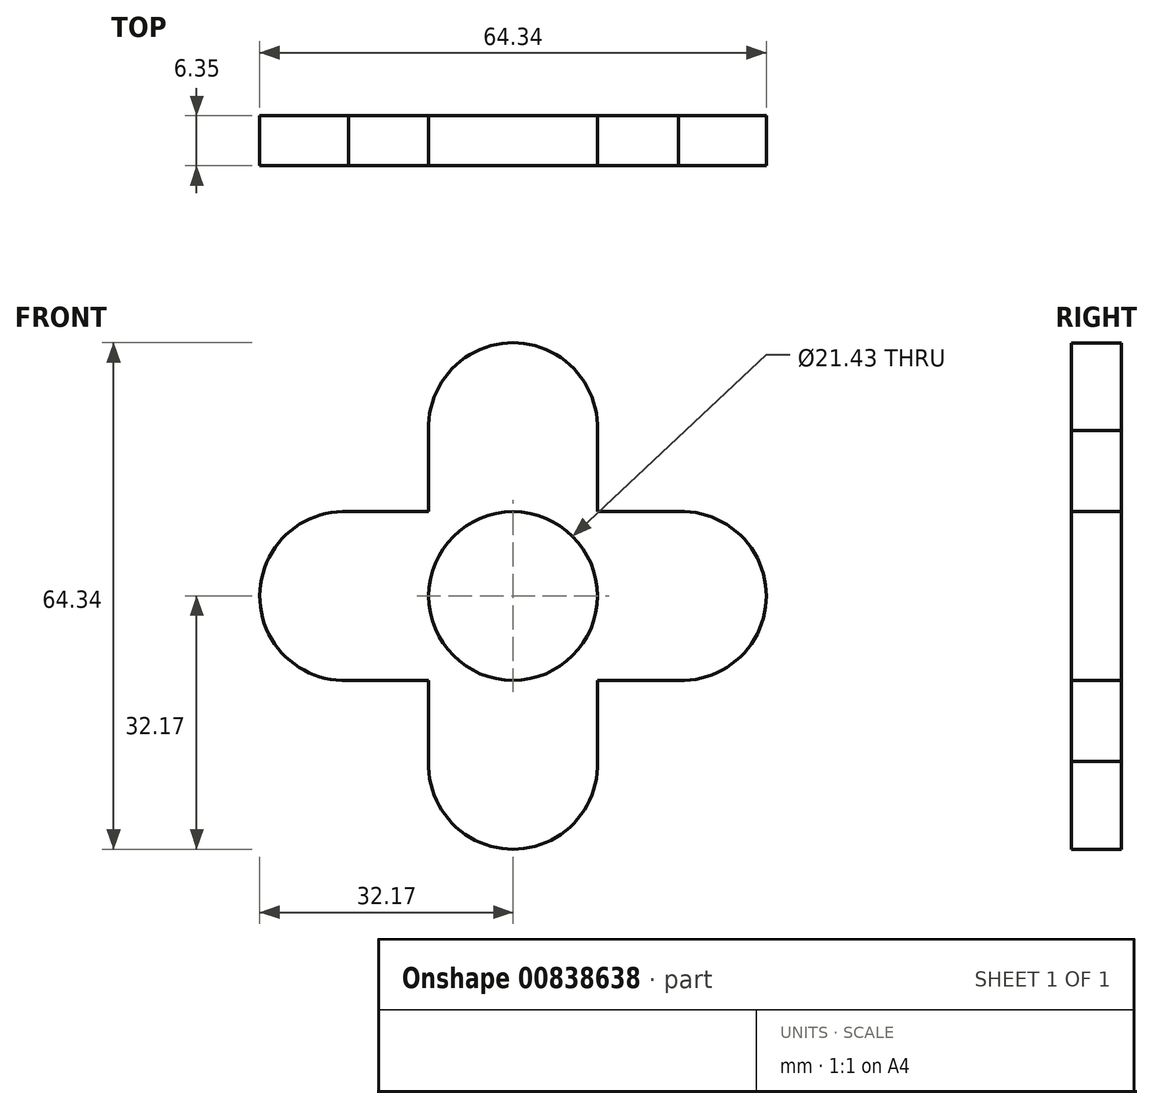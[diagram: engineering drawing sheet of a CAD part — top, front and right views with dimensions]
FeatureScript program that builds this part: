
annotation { "Feature Type Name" : "Feature", "Feature Type Description" : "" }
export const myFeature = defineFeature(function(context is Context, id is Id, definition is map)
    precondition{}
    {
        {
            var Q0;
            Q0=qCreatedBy(makeId("Front.planeOp"),FACE);
            var sketch = newSketch(context, id + "F0", { "sketchPlane" : qUnion([Q0])});
            skCircle(sketch, "E0", {"center": v(0, 0) * mm, "radius": 25.4 * mm});
            skSolve(sketch);
        }
        {
            var Q0;
            Q0=makeQuery(id+"F0.imprint","IMPRINT",FACE,{"disambiguationData":[TD([[makeQuery(id+"F0.imprint","IMPRINT",EDGE,{"derivedFrom":sQuery(id+"F0.wireOp",EDGE,"E0")}),1.0]])]});
            extrude(context, id + "F1", {"entities" : qUnion([Q0]), "depth" : 6.35 * mm, "offsetDistance" : 25.4 * mm});
        }
        {
            var Q0;
            Q0=makeQuery(id+"F1.opExtrude","CAP_FACE",FACE,{"disambiguationData":[OSD([sQuery(id+"F0.wireOp",EDGE,"E0")])],"isStart":false});
            var sketch = newSketch(context, id + "F2", { "sketchPlane" : qUnion([Q0])});
            skCircle(sketch, "E1", {"center": v(0, 0) * mm, "radius": 10.72 * mm});
            skSolve(sketch);
        }
        {
            var Q0;
            Q0=makeQuery(id+"F2.imprint","IMPRINT",FACE,{"disambiguationData":[TD([[makeQuery(id+"F2.imprint","IMPRINT",EDGE,{"derivedFrom":sQuery(id+"F2.wireOp",EDGE,"E1")}),1.0]])]});
            extrude(context, id + "F3", {"entities" : qUnion([Q0]), "operationType" : NewBodyOperationType.REMOVE, "endBound" : BoundingType.THROUGH_ALL, "oppositeDirection" : true, "depth" : 25.4 * mm, "offsetDistance" : 25.4 * mm});
        }
        {
            var Q0;
            Q0=makeQuery(id+"F1.opExtrude","CAP_FACE",FACE,{"disambiguationData":[OSD([sQuery(id+"F0.wireOp",EDGE,"E0")])],"isStart":false});
            var sketch = newSketch(context, id + "F4", { "sketchPlane" : qUnion([Q0])});
            skLineSegment(sketch, "E2", {"start": v(-10.72, 0) * mm, "end": v(-10.72, 25.4) * mm});
            skLineSegment(sketch, "E3", {"start": v(-10.72, 25.4) * mm, "end": v(10.72, 25.4) * mm});
            skLineSegment(sketch, "E4", {"start": v(10.72, 25.4) * mm, "end": v(10.72, 0) * mm});
            skLineSegment(sketch, "E5", {"start": v(10.72, 0) * mm, "end": v(10.72, -25.4) * mm});
            skLineSegment(sketch, "E6", {"start": v(10.72, -25.4) * mm, "end": v(-10.72, -25.4) * mm});
            skLineSegment(sketch, "E7", {"start": v(-10.72, -25.4) * mm, "end": v(-10.72, 0) * mm});
            skLineSegment(sketch, "E8", {"start": v(0, 10.72) * mm, "end": v(-25.4, 10.72) * mm});
            skLineSegment(sketch, "E9", {"start": v(-25.4, 10.72) * mm, "end": v(-25.4, -10.72) * mm});
            skLineSegment(sketch, "E10", {"start": v(-25.4, -10.72) * mm, "end": v(0, -10.72) * mm});
            skLineSegment(sketch, "E11", {"start": v(0, -10.72) * mm, "end": v(25.4, -10.72) * mm});
            skLineSegment(sketch, "E12", {"start": v(25.4, -10.72) * mm, "end": v(25.4, 10.72) * mm});
            skLineSegment(sketch, "E13", {"start": v(25.4, 10.72) * mm, "end": v(0, 10.72) * mm});
            skLineSegment(sketch, "E14", {"start": v(-25.4, 10.72) * mm, "end": v(10.72, 25.4) * mm});
            skLineSegment(sketch, "E15", {"start": v(-10.72, 25.4) * mm, "end": v(25.4, 10.72) * mm});
            skLineSegment(sketch, "E16", {"start": v(10.72, 25.4) * mm, "end": v(25.4, -10.72) * mm});
            skLineSegment(sketch, "E17", {"start": v(25.4, 10.72) * mm, "end": v(10.72, -25.4) * mm});
            skLineSegment(sketch, "E18", {"start": v(-25.4, -10.72) * mm, "end": v(10.72, -25.4) * mm});
            skLineSegment(sketch, "E19", {"start": v(-10.72, -25.4) * mm, "end": v(25.4, -10.72) * mm});
            skLineSegment(sketch, "E20", {"start": v(-25.4, 10.72) * mm, "end": v(-10.72, -25.4) * mm});
            skLineSegment(sketch, "E21", {"start": v(-25.4, -10.72) * mm, "end": v(-10.72, 25.4) * mm});
            skLineSegment(sketch, "E22", {"start": v(-21.04, 0) * mm, "end": v(-21.05, 10.72) * mm});
            skLineSegment(sketch, "E23", {"start": v(-21.05, 10.72) * mm, "end": v(-21.04, -10.72) * mm});
            skLineSegment(sketch, "E24", {"start": v(0, 21.04) * mm, "end": v(10.72, 21.04) * mm});
            skLineSegment(sketch, "E25", {"start": v(10.72, 21.04) * mm, "end": v(-10.72, 21.04) * mm});
            skLineSegment(sketch, "E26", {"start": v(21.04, 0) * mm, "end": v(21.04, 10.72) * mm});
            skLineSegment(sketch, "E27", {"start": v(21.04, 10.72) * mm, "end": v(21.05, -10.72) * mm});
            skLineSegment(sketch, "E28", {"start": v(0, -21.04) * mm, "end": v(-10.72, -21.04) * mm});
            skLineSegment(sketch, "E29", {"start": v(-10.72, -21.04) * mm, "end": v(10.72, -21.04) * mm});
            skCircle(sketch, "E30", {"center": v(0, -21.44) * mm, "radius": 10.73 * mm});
            skCircle(sketch, "E31", {"center": v(-21.45, 0) * mm, "radius": 10.73 * mm});
            skCircle(sketch, "E32", {"center": v(0, 21.44) * mm, "radius": 10.73 * mm});
            skCircle(sketch, "E33", {"center": v(21.45, 0) * mm, "radius": 10.73 * mm});
            skSolve(sketch);
        }
        {
            var Q0;
            {var subQ0=sQuery(id+"F4.wireOp",EDGE,"E31");var subQ1=sQuery(id+"F4.wireOp",EDGE,"E8");var subQ2=makeQuery(id+"F4.imprint","INTERSECT",VERTEX,{"disambiguationData":[OD(1.0)],"derivedFrom":[subQ1,subQ0]});Q0=makeQuery(id+"F4.imprint","IMPRINT",FACE,{"disambiguationData":[TD([[makeQuery(id+"F4.imprint","IMPRINT",EDGE,{"disambiguationData":[TD([[subQ2,-1.0]])],"derivedFrom":subQ1}),1.0]])]});}
            var Q1;
            {var subQ0=sQuery(id+"F4.wireOp",EDGE,"E31");var subQ1=sQuery(id+"F4.wireOp",EDGE,"E10");var subQ2=makeQuery(id+"F4.imprint","INTERSECT",VERTEX,{"disambiguationData":[OD(0.0)],"derivedFrom":[subQ1,subQ0]});Q1=makeQuery(id+"F4.imprint","IMPRINT",FACE,{"disambiguationData":[TD([[makeQuery(id+"F4.imprint","IMPRINT",EDGE,{"disambiguationData":[TD([[subQ2,1.0]])],"derivedFrom":subQ1}),1.0]])]});}
            var Q2;
            {var subQ0=sQuery(id+"F4.wireOp",EDGE,"E30");var subQ1=sQuery(id+"F4.wireOp",EDGE,"E7");var subQ2=makeQuery(id+"F4.imprint","INTERSECT",VERTEX,{"derivedFrom":[subQ1,subQ0]});Q2=makeQuery(id+"F4.imprint","IMPRINT",FACE,{"disambiguationData":[TD([[makeQuery(id+"F4.imprint","IMPRINT",EDGE,{"disambiguationData":[TD([[subQ2,1.0]])],"derivedFrom":subQ1}),-1.0]])]});}
            var Q3;
            {var subQ0=sQuery(id+"F4.wireOp",EDGE,"E30");var subQ1=sQuery(id+"F4.wireOp",EDGE,"E5");var subQ2=makeQuery(id+"F4.imprint","INTERSECT",VERTEX,{"derivedFrom":[subQ1,subQ0]});Q3=makeQuery(id+"F4.imprint","IMPRINT",FACE,{"disambiguationData":[TD([[makeQuery(id+"F4.imprint","IMPRINT",EDGE,{"disambiguationData":[TD([[subQ2,-1.0]])],"derivedFrom":subQ1}),-1.0]])]});}
            var Q4;
            {var subQ0=sQuery(id+"F4.wireOp",EDGE,"E33");var subQ1=sQuery(id+"F4.wireOp",EDGE,"E11");var subQ2=makeQuery(id+"F4.imprint","INTERSECT",VERTEX,{"derivedFrom":[subQ1,subQ0]});Q4=makeQuery(id+"F4.imprint","IMPRINT",FACE,{"disambiguationData":[TD([[makeQuery(id+"F4.imprint","IMPRINT",EDGE,{"disambiguationData":[TD([[subQ2,-1.0]])],"derivedFrom":subQ1}),1.0]])]});}
            var Q5;
            {var subQ0=sQuery(id+"F4.wireOp",EDGE,"E33");var subQ1=sQuery(id+"F4.wireOp",EDGE,"E13");var subQ2=makeQuery(id+"F4.imprint","INTERSECT",VERTEX,{"derivedFrom":[subQ1,subQ0]});Q5=makeQuery(id+"F4.imprint","IMPRINT",FACE,{"disambiguationData":[TD([[makeQuery(id+"F4.imprint","IMPRINT",EDGE,{"disambiguationData":[TD([[subQ2,1.0]])],"derivedFrom":subQ1}),1.0]])]});}
            var Q6;
            {var subQ0=sQuery(id+"F4.wireOp",EDGE,"E32");var subQ1=sQuery(id+"F4.wireOp",EDGE,"E4");var subQ2=makeQuery(id+"F4.imprint","INTERSECT",VERTEX,{"derivedFrom":[subQ1,subQ0]});Q6=makeQuery(id+"F4.imprint","IMPRINT",FACE,{"disambiguationData":[TD([[makeQuery(id+"F4.imprint","IMPRINT",EDGE,{"disambiguationData":[TD([[subQ2,1.0]])],"derivedFrom":subQ1}),-1.0]])]});}
            var Q7;
            {var subQ0=sQuery(id+"F4.wireOp",EDGE,"E32");var subQ1=sQuery(id+"F4.wireOp",EDGE,"E2");var subQ2=makeQuery(id+"F4.imprint","INTERSECT",VERTEX,{"derivedFrom":[subQ1,subQ0]});Q7=makeQuery(id+"F4.imprint","IMPRINT",FACE,{"disambiguationData":[TD([[makeQuery(id+"F4.imprint","IMPRINT",EDGE,{"disambiguationData":[TD([[subQ2,-1.0]])],"derivedFrom":subQ1}),-1.0]])]});}
            var Q8;
            {var subQ1=sQuery(id+"F4.wireOp",EDGE,"E2");var subQ7=sQuery(id+"F4.wireOp",EDGE,"E32");var subQ9=makeQuery(id+"F4.imprint","INTERSECT",VERTEX,{"derivedFrom":[subQ1,subQ7]});Q8=makeQuery(id+"F4.imprint","IMPRINT",FACE,{"disambiguationData":[TD([[makeQuery(id+"F4.imprint","IMPRINT",EDGE,{"disambiguationData":[TD([[subQ9,-1.0]])],"derivedFrom":subQ1}),1.0]])]});}
            var Q9;
            {var subQ0=sQuery(id+"F4.wireOp",EDGE,"E21");var subQ1=sQuery(id+"F4.wireOp",EDGE,"E14");var subQ2=makeQuery(id+"F4.imprint","INTERSECT",VERTEX,{"derivedFrom":[subQ1,subQ0]});Q9=makeQuery(id+"F4.imprint","IMPRINT",FACE,{"disambiguationData":[TD([[makeQuery(id+"F4.imprint","IMPRINT",EDGE,{"disambiguationData":[TD([[subQ2,1.0]])],"derivedFrom":subQ1}),1.0]])]});}
            var Q10;
            {var subQ0=sQuery(id+"F4.wireOp",EDGE,"E21");var subQ1=sQuery(id+"F4.wireOp",EDGE,"E8");var subQ2=makeQuery(id+"F4.imprint","INTERSECT",VERTEX,{"derivedFrom":[subQ1,subQ0]});Q10=makeQuery(id+"F4.imprint","IMPRINT",FACE,{"disambiguationData":[TD([[makeQuery(id+"F4.imprint","IMPRINT",EDGE,{"disambiguationData":[TD([[subQ2,-1.0]])],"derivedFrom":subQ1}),-1.0]])]});}
            var Q11;
            {var subQ0=sQuery(id+"F4.wireOp",EDGE,"E8");var subQ1=sQuery(id+"F4.wireOp",EDGE,"E2");var subQ2=makeQuery(id+"F4.imprint","INTERSECT",VERTEX,{"derivedFrom":[subQ1,subQ0]});Q11=makeQuery(id+"F4.imprint","IMPRINT",FACE,{"disambiguationData":[TD([[makeQuery(id+"F4.imprint","IMPRINT",EDGE,{"disambiguationData":[TD([[subQ2,-1.0]])],"derivedFrom":subQ1}),1.0]])]});}
            var Q12;
            {var subQ5=sQuery(id+"F4.wireOp",EDGE,"E32");var subQ6=sQuery(id+"F4.wireOp",EDGE,"E4");var subQ9=makeQuery(id+"F4.imprint","INTERSECT",VERTEX,{"derivedFrom":[subQ6,subQ5]});Q12=makeQuery(id+"F4.imprint","IMPRINT",FACE,{"disambiguationData":[TD([[makeQuery(id+"F4.imprint","IMPRINT",EDGE,{"disambiguationData":[TD([[subQ9,1.0]])],"derivedFrom":subQ6}),1.0]])]});}
            var Q13;
            {var subQ0=sQuery(id+"F4.wireOp",EDGE,"E16");var subQ1=sQuery(id+"F4.wireOp",EDGE,"E15");var subQ2=makeQuery(id+"F4.imprint","INTERSECT",VERTEX,{"derivedFrom":[subQ1,subQ0]});Q13=makeQuery(id+"F4.imprint","IMPRINT",FACE,{"disambiguationData":[TD([[makeQuery(id+"F4.imprint","IMPRINT",EDGE,{"disambiguationData":[TD([[subQ2,-1.0]])],"derivedFrom":subQ1}),1.0]])]});}
            var Q14;
            {var subQ0=sQuery(id+"F4.wireOp",EDGE,"E15");var subQ1=sQuery(id+"F4.wireOp",EDGE,"E4");var subQ2=makeQuery(id+"F4.imprint","INTERSECT",VERTEX,{"derivedFrom":[subQ1,subQ0]});Q14=makeQuery(id+"F4.imprint","IMPRINT",FACE,{"disambiguationData":[TD([[makeQuery(id+"F4.imprint","IMPRINT",EDGE,{"disambiguationData":[TD([[subQ2,-1.0]])],"derivedFrom":subQ1}),1.0]])]});}
            var Q15;
            {var subQ5=sQuery(id+"F4.wireOp",EDGE,"E13");var subQ7=sQuery(id+"F4.wireOp",EDGE,"E33");var subQ10=makeQuery(id+"F4.imprint","INTERSECT",VERTEX,{"derivedFrom":[subQ5,subQ7]});Q15=makeQuery(id+"F4.imprint","IMPRINT",FACE,{"disambiguationData":[TD([[makeQuery(id+"F4.imprint","IMPRINT",EDGE,{"disambiguationData":[TD([[subQ10,1.0]])],"derivedFrom":subQ5}),-1.0]])]});}
            var Q16;
            {var subQ5=sQuery(id+"F4.wireOp",EDGE,"E31");var subQ6=sQuery(id+"F4.wireOp",EDGE,"E10");var subQ9=makeQuery(id+"F4.imprint","INTERSECT",VERTEX,{"disambiguationData":[OD(0.0)],"derivedFrom":[subQ6,subQ5]});Q16=makeQuery(id+"F4.imprint","IMPRINT",FACE,{"disambiguationData":[TD([[makeQuery(id+"F4.imprint","IMPRINT",EDGE,{"disambiguationData":[TD([[subQ9,1.0]])],"derivedFrom":subQ6}),-1.0]])]});}
            var Q17;
            {var subQ0=sQuery(id+"F4.wireOp",EDGE,"E18");var subQ1=sQuery(id+"F4.wireOp",EDGE,"E7");var subQ2=makeQuery(id+"F4.imprint","INTERSECT",VERTEX,{"derivedFrom":[subQ1,subQ0]});Q17=makeQuery(id+"F4.imprint","IMPRINT",FACE,{"disambiguationData":[TD([[makeQuery(id+"F4.imprint","IMPRINT",EDGE,{"disambiguationData":[TD([[subQ2,-1.0]])],"derivedFrom":subQ1}),1.0]])]});}
            var Q18;
            {var subQ0=sQuery(id+"F4.wireOp",EDGE,"E20");var subQ1=sQuery(id+"F4.wireOp",EDGE,"E18");var subQ2=makeQuery(id+"F4.imprint","INTERSECT",VERTEX,{"derivedFrom":[subQ1,subQ0]});Q18=makeQuery(id+"F4.imprint","IMPRINT",FACE,{"disambiguationData":[TD([[makeQuery(id+"F4.imprint","IMPRINT",EDGE,{"disambiguationData":[TD([[subQ2,1.0]])],"derivedFrom":subQ1}),-1.0]])]});}
            var Q19;
            {var subQ5=sQuery(id+"F4.wireOp",EDGE,"E7");var subQ7=sQuery(id+"F4.wireOp",EDGE,"E30");var subQ8=makeQuery(id+"F4.imprint","INTERSECT",VERTEX,{"derivedFrom":[subQ5,subQ7]});Q19=makeQuery(id+"F4.imprint","IMPRINT",FACE,{"disambiguationData":[TD([[makeQuery(id+"F4.imprint","IMPRINT",EDGE,{"disambiguationData":[TD([[subQ8,1.0]])],"derivedFrom":subQ5}),1.0]])]});}
            var Q20;
            {var subQ0=sQuery(id+"F4.wireOp",EDGE,"E11");var subQ1=sQuery(id+"F4.wireOp",EDGE,"E5");var subQ2=makeQuery(id+"F4.imprint","INTERSECT",VERTEX,{"derivedFrom":[subQ1,subQ0]});Q20=makeQuery(id+"F4.imprint","IMPRINT",FACE,{"disambiguationData":[TD([[makeQuery(id+"F4.imprint","IMPRINT",EDGE,{"disambiguationData":[TD([[subQ2,-1.0]])],"derivedFrom":subQ1}),1.0]])]});}
            var Q21;
            {var subQ1=sQuery(id+"F4.wireOp",EDGE,"E5");var subQ7=sQuery(id+"F4.wireOp",EDGE,"E30");var subQ8=makeQuery(id+"F4.imprint","INTERSECT",VERTEX,{"derivedFrom":[subQ1,subQ7]});Q21=makeQuery(id+"F4.imprint","IMPRINT",FACE,{"disambiguationData":[TD([[makeQuery(id+"F4.imprint","IMPRINT",EDGE,{"disambiguationData":[TD([[subQ8,-1.0]])],"derivedFrom":subQ1}),1.0]])]});}
            var Q22;
            {var subQ0=sQuery(id+"F4.wireOp",EDGE,"E19");var subQ1=sQuery(id+"F4.wireOp",EDGE,"E17");var subQ2=makeQuery(id+"F4.imprint","INTERSECT",VERTEX,{"derivedFrom":[subQ1,subQ0]});Q22=makeQuery(id+"F4.imprint","IMPRINT",FACE,{"disambiguationData":[TD([[makeQuery(id+"F4.imprint","IMPRINT",EDGE,{"disambiguationData":[TD([[subQ2,-1.0]])],"derivedFrom":subQ1}),1.0]])]});}
            var Q23;
            {var subQ5=sQuery(id+"F4.wireOp",EDGE,"E11");var subQ7=sQuery(id+"F4.wireOp",EDGE,"E33");var subQ8=makeQuery(id+"F4.imprint","INTERSECT",VERTEX,{"derivedFrom":[subQ5,subQ7]});Q23=makeQuery(id+"F4.imprint","IMPRINT",FACE,{"disambiguationData":[TD([[makeQuery(id+"F4.imprint","IMPRINT",EDGE,{"disambiguationData":[TD([[subQ8,-1.0]])],"derivedFrom":subQ5}),-1.0]])]});}
            extrude(context, id + "F5", {"entities" : qUnion([Q0, Q1, Q2, Q3, Q4, Q5, Q6, Q7, Q8, Q9, Q10, Q11, Q12, Q13, Q14, Q15, Q16, Q17, Q18, Q19, Q20, Q21, Q22, Q23]), "operationType" : NewBodyOperationType.REMOVE, "endBound" : BoundingType.THROUGH_ALL, "oppositeDirection" : true, "depth" : 25.4 * mm, "offsetDistance" : 25.4 * mm});
        }
        {
            var Q0;
            Q0=makeQuery(id+"F1.opExtrude","CAP_FACE",FACE,{"disambiguationData":[OSD([sQuery(id+"F0.wireOp",EDGE,"E0")])],"isStart":false});
            var sketch = newSketch(context, id + "F6", { "sketchPlane" : qUnion([Q0])});
            skCircle(sketch, "E34", {"center": v(0, 21.44) * mm, "radius": 10.73 * mm});
            skPoint(sketch, "E34.first.point", {"position": v(-10.6, 23.08) * mm});
            skPoint(sketch, "E34.second.point", {"position": v(10.6, 23.08) * mm});
            skPoint(sketch, "E34.third.point", {"position": v(10.72, 21.04) * mm});
            skCircle(sketch, "E35", {"center": v(-21.45, 0) * mm, "radius": 10.73 * mm});
            skPoint(sketch, "E35.first.point", {"position": v(-23.08, 10.6) * mm});
            skPoint(sketch, "E35.second.point", {"position": v(-23.08, -10.6) * mm});
            skPoint(sketch, "E35.third.point", {"position": v(-21.01, -10.72) * mm});
            skCircle(sketch, "E36", {"center": v(21.45, 0) * mm, "radius": 10.73 * mm});
            skPoint(sketch, "E36.first.point", {"position": v(23.08, 10.6) * mm});
            skPoint(sketch, "E36.second.point", {"position": v(23.08, -10.6) * mm});
            skPoint(sketch, "E36.third.point", {"position": v(21.05, -10.72) * mm});
            skCircle(sketch, "E37", {"center": v(0, -21.44) * mm, "radius": 10.73 * mm});
            skPoint(sketch, "E37.first.point", {"position": v(-10.6, -23.08) * mm});
            skPoint(sketch, "E37.second.point", {"position": v(10.6, -23.08) * mm});
            skPoint(sketch, "E37.third.point", {"position": v(10.72, -21.04) * mm});
            skSolve(sketch);
        }
        {
            var Q0;
            {var subQ1=sQuery(id+"F0.wireOp",EDGE,"E0");var subQ2=sQuery(id+"F4.wireOp",EDGE,"E31");var subQ3=sQuery(id+"F4.wireOp",EDGE,"E8");var subQ4=makeQuery(id+"F4.imprint","INTERSECT",VERTEX,{"disambiguationData":[OD(1.0)],"derivedFrom":[subQ3,subQ2]});var subQ5=makeQuery(id+"F1.opExtrude","CAP_EDGE",EDGE,{"disambiguationData":[OSD([subQ1])],"isStart":false});var subQ6=sQuery(id+"F4.wireOp",EDGE,"E23");var subQ7=makeQuery(id+"F4.imprint","INTERSECT",VERTEX,{"disambiguationData":[OD(0.0)],"derivedFrom":[subQ6,subQ2]});var subQ11=makeQuery(id+"F5.boolean.opBoolean","SPLIT",EDGE,{"disambiguationData":[TD([makeQuery(id+"F5.opExtrude","SWEPT_FACE",FACE,{"disambiguationData":[OSD([subQ2]),TDD([makeQuery(id+"F4.imprint","IMPRINT",EDGE,{"disambiguationData":[TD([[subQ7,1.0]])],"derivedFrom":subQ2}),makeQuery(id+"F4.imprint","IMPRINT",EDGE,{"disambiguationData":[TD([[subQ7,-1.0]])],"derivedFrom":subQ2}),makeQuery(id+"F4.imprint","IMPRINT",EDGE,{"disambiguationData":[TD([[subQ4,-1.0]])],"derivedFrom":subQ2})])]})])],"derivedFrom":subQ5});Q0=makeQuery(id+"F6.imprint","IMPRINT",FACE,{"disambiguationData":[TD([[makeQuery(id+"F6.imprint","IMPRINT",EDGE,{"derivedFrom":subQ11}),-1.0]])]});}
            var Q1;
            {var subQ1=sQuery(id+"F0.wireOp",EDGE,"E0");var subQ2=sQuery(id+"F4.wireOp",EDGE,"E32");var subQ3=sQuery(id+"F4.wireOp",EDGE,"E25");var subQ4=sQuery(id+"F4.wireOp",EDGE,"E4");var subQ5=makeQuery(id+"F4.imprint","INTERSECT",VERTEX,{"derivedFrom":[subQ4,subQ2]});var subQ6=makeQuery(id+"F1.opExtrude","CAP_EDGE",EDGE,{"disambiguationData":[OSD([subQ1])],"isStart":false});var subQ9=makeQuery(id+"F5.boolean.opBoolean","SPLIT",EDGE,{"disambiguationData":[TD([makeQuery(id+"F5.opExtrude","SWEPT_FACE",FACE,{"disambiguationData":[OSD([subQ2]),TDD([makeQuery(id+"F4.imprint","IMPRINT",EDGE,{"disambiguationData":[TD([[subQ5,-1.0],[makeQuery(id+"F4.imprint","INTERSECT",VERTEX,{"disambiguationData":[OD(0.0)],"derivedFrom":[subQ6,subQ2]}),1.0]])],"derivedFrom":subQ2}),makeQuery(id+"F4.imprint","IMPRINT",EDGE,{"disambiguationData":[TD([[makeQuery(id+"F4.imprint","INTERSECT",VERTEX,{"derivedFrom":[subQ4,subQ3,subQ2]}),-1.0],[subQ5,1.0]])],"derivedFrom":subQ2})])]})])],"derivedFrom":subQ6});Q1=makeQuery(id+"F6.imprint","IMPRINT",FACE,{"disambiguationData":[TD([[makeQuery(id+"F6.imprint","IMPRINT",EDGE,{"derivedFrom":subQ9}),-1.0]])]});}
            var Q2;
            {var subQ1=sQuery(id+"F0.wireOp",EDGE,"E0");var subQ2=sQuery(id+"F4.wireOp",EDGE,"E33");var subQ5=makeQuery(id+"F1.opExtrude","CAP_EDGE",EDGE,{"disambiguationData":[OSD([subQ1])],"isStart":false});var subQ7=sQuery(id+"F4.wireOp",EDGE,"E13");var subQ8=makeQuery(id+"F4.imprint","INTERSECT",VERTEX,{"derivedFrom":[subQ7,subQ2]});var subQ9=makeQuery(id+"F5.boolean.opBoolean","SPLIT",EDGE,{"disambiguationData":[TD([makeQuery(id+"F5.opExtrude","SWEPT_FACE",FACE,{"disambiguationData":[OSD([subQ2]),TDD([makeQuery(id+"F4.imprint","IMPRINT",EDGE,{"disambiguationData":[TD([[subQ8,1.0]])],"derivedFrom":subQ2}),makeQuery(id+"F4.imprint","IMPRINT",EDGE,{"disambiguationData":[TD([[subQ8,-1.0]])],"derivedFrom":subQ2})])]})])],"derivedFrom":subQ5});Q2=makeQuery(id+"F6.imprint","IMPRINT",FACE,{"disambiguationData":[TD([[makeQuery(id+"F6.imprint","IMPRINT",EDGE,{"derivedFrom":subQ9}),-1.0]])]});}
            var Q3;
            {var subQ1=sQuery(id+"F0.wireOp",EDGE,"E0");var subQ2=sQuery(id+"F4.wireOp",EDGE,"E30");var subQ3=sQuery(id+"F4.wireOp",EDGE,"E7");var subQ4=makeQuery(id+"F4.imprint","INTERSECT",VERTEX,{"derivedFrom":[subQ3,subQ2]});var subQ5=makeQuery(id+"F1.opExtrude","CAP_EDGE",EDGE,{"disambiguationData":[OSD([subQ1])],"isStart":false});var subQ8=makeQuery(id+"F5.boolean.opBoolean","SPLIT",EDGE,{"disambiguationData":[TD([makeQuery(id+"F5.opExtrude","SWEPT_FACE",FACE,{"disambiguationData":[OSD([subQ2]),TDD([makeQuery(id+"F4.imprint","IMPRINT",EDGE,{"disambiguationData":[TD([[makeQuery(id+"F4.imprint","INTERSECT",VERTEX,{"derivedFrom":[subQ3,sQuery(id+"F4.wireOp",EDGE,"E28"),subQ2]}),-1.0],[subQ4,1.0]])],"derivedFrom":subQ2}),makeQuery(id+"F4.imprint","IMPRINT",EDGE,{"disambiguationData":[TD([[subQ4,-1.0],[makeQuery(id+"F4.imprint","INTERSECT",VERTEX,{"disambiguationData":[OD(0.0)],"derivedFrom":[subQ5,subQ2]}),1.0]])],"derivedFrom":subQ2})])]})])],"derivedFrom":subQ5});Q3=makeQuery(id+"F6.imprint","IMPRINT",FACE,{"disambiguationData":[TD([[makeQuery(id+"F6.imprint","IMPRINT",EDGE,{"derivedFrom":subQ8}),-1.0]])]});}
            extrude(context, id + "F7", {"entities" : qUnion([Q0, Q1, Q2, Q3]), "operationType" : NewBodyOperationType.ADD, "oppositeDirection" : true, "depth" : 6.35 * mm, "offsetDistance" : 25.4 * mm});
        }
    });
